# Revit family: puzg-mp2m_2_60hz
name_source: partatom
category: 機械設備
units: mm (PartAtom-declared; Revit-internal decimal feet)

## family parameters
OmniClass タイトル = Split System Air Conditioning Units
OmniClass 番号 = 23.75.10.24.21.27.27
パーツ タイプ = 標準
ロード時にボイドで切り取り = いいえ
丸型コネクタ寸法 = 直径を使用
作業面ベース = いいえ
共有 = いいえ
常に垂直 = はい
部屋計算ポイント = いいえ

## types (2) — shared parameters
Clearance Back = 100  [stored 0.328084 ft]
Clearance Front = 500  [stored 1.64042 ft]
Clearance Left = 100  [stored 0.328084 ft]
Clearance Right = 350  [stored 1.14829 ft]
Clearance Top = 1000  [stored 3.28084 ft]
Depth = 300
Height = 630  [stored 2.06693 ft]
IfcExportAs = IfcUnitaryEquipmentType
IfcExportType = AIRCONDITIONINGUNIT
OmniClassCode = 23-33 17 13 11
URL = https://www.mitsubishielectric.co.jp
Uniclass2015Code = Pr_70_65_03_84
Uniclass2015Title = Split coil remote air cooled condensing units
Uniclass2015Version = Systems v1.9
Width = 809  [stored 2.6542 ft]
アンカーボルト位置X = 500  [stored 1.64042 ft]
アンカーボルト位置Y = 330  [stored 1.08268 ft]
サービススペース = はい
ドレン　位置X = 404.5  [stored 1.3271 ft]
ドレン　位置Y = 48.5  [stored 0.159121 ft]
ドレン　位置Z = 8.5  [stored 0.0278871 ft]
ドレン管径 = 42.00 mm
ユニット2 = はい
ユニット3 = はい
ユニット数 = 1
仕様書バージョン = Version1.0
企業コード = 108420
冷媒ガス管径 = 12.70 mm
冷媒液管径 = 6.35 mm
冷媒管位置X = 420  [stored 1.37795 ft]
冷媒管位置Y = 153.75  [stored 0.504429 ft]
冷媒管位置Z = 158.95
冷媒管径 = 60.00 mm
冷媒管径符号 = Ac
冷媒管（ガス）位置X = 420  [stored 1.37795 ft]
冷媒管（ガス）位置Y = 153.75  [stored 0.504429 ft]
冷媒管（液）位置X = 420  [stored 1.37795 ft]
冷媒管（液）位置Y = 153.75  [stored 0.504429 ft]
冷房能力 = 5 kW
分類コード = 50053003126100
参照している仕様書等のバージョン = 公共建築物標準仕様書（機械設備工事編）平成31年度版
周波数 = 60 Hz
呼称 = パッケージ形空気調和機_室外機
始動方式 = インバータ始動方式
形名 = PUZ-ZRMP-1
形式 = パッケージ形 室外機
推奨ブレーカー容量 = 15 A
最大電流値 = 9 A
最小電線太さ_mm2 = 1.6
本体マテリアル = <カテゴリ別>
極数 = 3
法定耐用年数 = 6
消費電力 = 0 kW
消費電力_冷房 = 0 kW
消費電力_暖房 = 0 kW
発停方法 = 付属スイッチ
相 = 3
積算_科目 = 1 空気調和設備
符号 = PAC
製品出荷対象 = 国内
製品質量 = 39.00 kg
製造元 = 三菱電機株式会社
設置方法 = 床置形
説明 = 空冷H/P PAC インバータ室外機
負荷分類 = 1_熱源類
質量 = 46.80 kg
運転質量 = 0.00 kg
電動機出力_圧縮機 = 1 kW
電動機出力_送風機 = 0 kW
電圧 = 200 V
電源位置X = 400  [stored 1.31234 ft]
電源位置Y = 61  [stored 0.200131 ft]
電源位置Z = 497.7  [stored 1.63287 ft]
音響パワーレベル（冷）(dB) = 65
zero-valued in all types: APF, COP, Clearance Bottom, 価格, 据付ピッチ1

## per-type parameters (varying)
| type | 暖房能力 | 構成品番 | 運転方法 | 音響パワーレベル（暖）(dB) |
| 室外機_PUZG-MP2MKA2 | 6 kW | PUZG-MP2MKA2 | 冷暖切替 | 67 |
| 室外機_PUG-MP2MKA2 | 0 kW | PUG-MP2MKA2 | 冷房専用 | 0 |

note: [stored X ft] marks values corroborated as IEEE doubles in the binary element streams (Revit-internal decimal feet)
